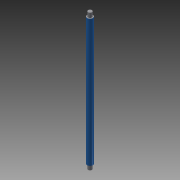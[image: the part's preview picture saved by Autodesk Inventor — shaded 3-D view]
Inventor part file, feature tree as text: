
AUTODESK INVENTOR PART (.ipt)
format: ipt  version: 2015 (Build 190159000, 159)  size: 77,824 bytes
history: native  units: mm
features: extrude x2, sketch x2, pattern_linear x1
ambient origin geometry x8: Origin, YZ Plane, XZ Plane, XY Plane, X Axis, Y Axis, Z Axis, Center Point
bodies: 实体1 (feature_tree)
feature tree (5):
  extrude  "拉伸1"  Depth=560.0mm TaperAngle=0.0deg
  extrude  "拉伸2"  Depth=20.0mm TaperAngle=0.0deg
  pattern_linear  "矩形阵列1"  Count1=2  [1 undecoded]
  sketch  "草图1"  dims[d0=25.0mm d1=560.0mm d2=0.0mm]
  sketch  "草图2"  dims[d3=17.0mm d4=20.0mm d5=0.0mm d6=20.0mm d8=580.0mm]
note: 1 required parameter value undecoded (feature->parameter linkage not recoverable at this tier; creation-order binding heuristic only, values carry confidence <= 0.55)
